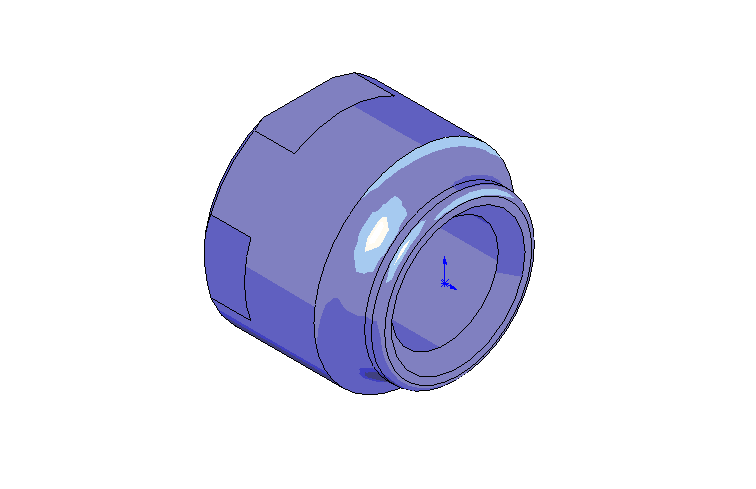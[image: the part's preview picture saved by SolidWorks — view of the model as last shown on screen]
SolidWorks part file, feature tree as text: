
SOLIDWORKS PART (.sldprt)
format: sldprt  version: not decoded by parser v0  size: 231,424 bytes
history: native  units: mm
features: plane x3, sketch x2, chamfer x2, material x1, revolve x1, fillet x1, cut_extrude x1 (+10 scaffold rows collapsed)
feature tree (21):
  scaffold x10  (default folders/planes/origin — collapsed)
  material  "Matériau <non spécifié>"
  plane  "Plan de face"
  plane  "Plan de dessus"
  plane  "Plan de droite"
  sketch  "Esquisse1"  dims[D1=5.0mm D2=8.0mm D3=17.0mm D4=12.0mm D5=15.0mm D6=1.0mm]
  revolve  "Révolution1"  Angle=360deg
  fillet  "Congé1"  Radius=0.5mm
  chamfer  "Chanfrein1"  Distance=1mm Angle=45deg
  chamfer  "Chanfrein2"  Distance=0.5mm Angle=45deg
  sketch  "Esquisse2"  dims[D1=14.0mm D2=13.0mm]
  cut_extrude  "Enlèv. mat.-Extru.1"  Depth=3.5mm
decode coverage: 7 of 7 modeling features carry decoded parameters
note: suppression state not decoded; provenance and decode notes live in map.json
